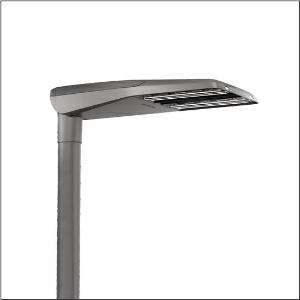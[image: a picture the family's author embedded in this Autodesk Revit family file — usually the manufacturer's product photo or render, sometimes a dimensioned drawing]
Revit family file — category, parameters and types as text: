
# Revit family: streetlight_sl_11_iq_midi___st1_0ab_5xc3n51f08le_f358
name_source: partatom
category: Lighting Fixtures
units: mm (PartAtom-declared; Revit-internal decimal feet)

## family parameters
Cut with Voids When Loaded = No
Host = Face
Light Source = No
Part Type = Normal
Room Calculation Point = No
Round Connector Dimension = Use Diameter
Shared = No

## types (1)
- --- (1 x LED, 7760 lm, 60.4 W, 3000K)
    Apparent Load = 60 VA
    CIE Flux Codes = 29 63 95 100 100
    Color Rendering = 70
    Color Temperature = 3000K
    Default Elevation = 1800 mm
    Description = Streetlight SL 11 iQ midi, mast luminaire, primary light control with 3 zone facetted reflector, of plastic, silver coated, highly specular, primary optical cover: cover, of PMMA, transparent, light distribution: ST1.0aB, light emission: direct distribution, primary light characteristic: asymmetric, installation type: post-top, side-entry, LED, High Power LED, rated luminous flux: 7.760lm, luminous efficacy: 129lm/W, light colour: 730, colour temperature: 3000K, control: optimised constant luminous flux control (CLO 2.0), Street-Remote, Desk-Remote (wireless, voltage-free reading and setting of iQ features in the workshop via application-optimized NFC function/RFID function), Light-Fading, Smart-Wire, Night-Set, Lumen-Switch, Temp-Guard, Auto-Match, with cable H07RN-F 5x 1.5mm², mains connection: 230..240V, AC, 50/60Hz, connection cable pre-assembled, cable length: 8,5m, start of lifetime: 60W, end of service life: 63W, reduction: 30W, luminaire housing, of diecast aluminium, powder-coated, Siteco® metallic grey (DB 702S), please order mast flange separately, inclination adjustable without tools: 0°, 5°, 10°, 15° (post-top) | 0°, -5°, -10°, -15° (side-entry), sealing non-destructively replaceable, multi-level sealing system, length: 780mm, width: 376mm, height: 118mm, mast flange for spigot size: 42mm (side-entry): 5XC10008XM4, 60/48mm (side-entry/post-top): 5XC10108XM2, 76/60mm (side-entry/post-top): 5XC10108XM1, equipment: standard, protection rating (complete): IP66, insulation class (complete): insulation class II (safety insulation), certification: CE, ENEC, VDE, impact resistance: IK09, permissible operating ambient temperature for outdoor applications: -25..+50°C, standard-compliant lighting for roads and squares, Environmental Product Declaration (EPD) tested and certified by an independent institute, packaging unit: 1 piece

Light Distribution: ST1.0aB
    Height = 118 mm
    Lamp = 1 x LED
    Lamp Light Flux = 7760 lm
    Lamp Power = 60.4 W
    Lamp count = 1
    Length = 780 mm
    Luminous efficacy = 128 lm/W
    Manufacturer = Siteco
    ModVariant = No
    Model = 5XC3N51F08LE
    Number of Poles = 1
    OnlyDefault = Yes
    Power Factor = 1
    Product Name = Streetlight SL 11 iQ midi | ST1.0aB
    Product group = mast luminaire | pylon top
    ProductGroupID = 6100
    Protection Class = Protection class II
    Protection Degree = IP 66
    RLX_Detail_Level = 1
    RLX_Emergency_Light_Flux = 0 lm
    RLX_Emergency_Type = 0
    RLX_Emergency_Type_DB = No
    RlxData = <blob elided: 70245 chars, md5=9535d6b0>
    Socket = socket
    Standby Power = 0 W
    System Light Flux = 7760 lm
    System Power = 60 W
    Type Comments = factory setting: luminous flux: 100 % | dim-lin: 254 | 520 mA
    Type Image = l_1005960.jpg
    URL = http://relux.com
    VarID = @adj_038861
    Voltage = 0 V
    Weight = 0.00 kg
    Width = 376 mm

## geometry (parser evidence)
native form markers: Blend x4, Sweep x12
no freeform markers — native parametric forms only
